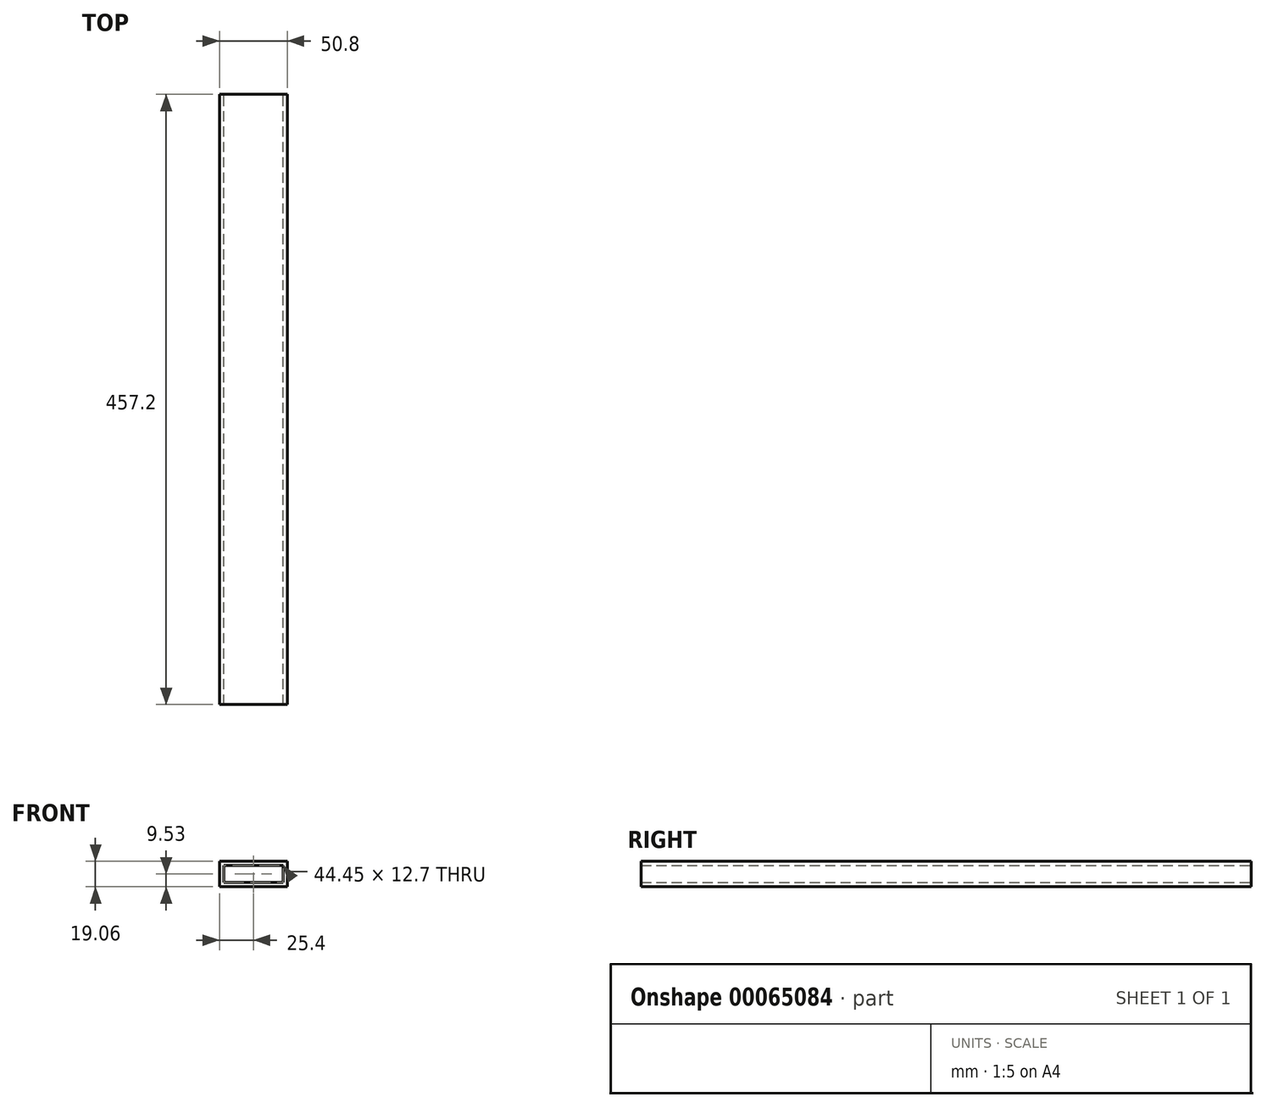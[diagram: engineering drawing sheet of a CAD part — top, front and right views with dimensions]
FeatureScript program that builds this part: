
annotation { "Feature Type Name" : "Feature", "Feature Type Description" : "" }
export const myFeature = defineFeature(function(context is Context, id is Id, definition is map)
    precondition{}
    {
        {
            var Q0;
            Q0=qCreatedBy(makeId("Front.planeOp"),FACE);
            var sketch = newSketch(context, id + "F0", { "sketchPlane" : qUnion([Q0])});
            skLineSegment(sketch, "E0.rect.bottom", {"start": v(-25.4, 9.53) * mm, "end": v(25.4, 9.53) * mm});
            skLineSegment(sketch, "E0.rect.top", {"start": v(-25.4, -9.53) * mm, "end": v(25.4, -9.53) * mm});
            skLineSegment(sketch, "E0.rect.left", {"start": v(-25.4, 9.53) * mm, "end": v(-25.4, -9.53) * mm});
            skLineSegment(sketch, "E0.rect.right", {"start": v(25.4, 9.53) * mm, "end": v(25.4, -9.53) * mm});
            skPoint(sketch, "E0.rect.middle", {"position": v(0, 0) * mm});
            skLineSegment(sketch, "E1.rect.bottom", {"start": v(-22.23, 6.35) * mm, "end": v(22.23, 6.35) * mm});
            skLineSegment(sketch, "E1.rect.top", {"start": v(-22.23, -6.35) * mm, "end": v(22.23, -6.35) * mm});
            skLineSegment(sketch, "E1.rect.left", {"start": v(-22.23, 6.35) * mm, "end": v(-22.23, -6.35) * mm});
            skLineSegment(sketch, "E1.rect.right", {"start": v(22.23, 6.35) * mm, "end": v(22.23, -6.35) * mm});
            skSolve(sketch);
        }
        {
            var Q0;
            Q0=makeQuery(id+"F0.imprint","IMPRINT",FACE,{"disambiguationData":[TD([[makeQuery(id+"F0.imprint","IMPRINT",EDGE,{"derivedFrom":sQuery(id+"F0.wireOp",EDGE,"E0.rect.bottom")}),-1.0]])]});
            extrude(context, id + "F1", {"entities" : qUnion([Q0]), "depth" : 457.2 * mm});
        }
    });
